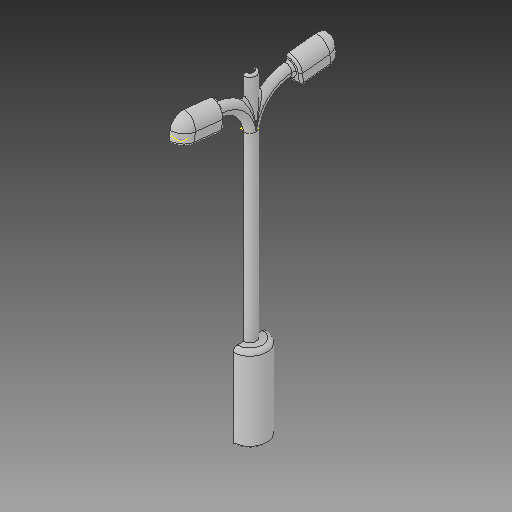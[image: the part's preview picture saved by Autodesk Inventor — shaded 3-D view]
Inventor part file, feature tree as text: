
AUTODESK INVENTOR PART (.ipt)
format: ipt  version: 2018 (Build 220112000, 112)  size: 484,864 bytes
history: native  units: mm
features: sketch x10, extrude x8, fillet x5, projected_geometry x3, plane x2, revolve x1, sweep x1, mirror x1
ambient origin geometry x8: Origin, YZ Plane, XZ Plane, XY Plane, X Axis, Y Axis, Z Axis, Center Point
bodies: Solid1 (feature_tree)
feature tree (31):
  revolve  "Revolution1"  [1 undecoded]
  fillet  "Fillet1"  Radius=8.0mm
  fillet  "Fillet2"  Radius=40.0mm
  fillet  "Fillet3"  [1 undecoded]
  plane  "Work Plane1"
  sweep  "Sweep1"
  extrude  "Extrusion2"  Depth=1.5mm
  fillet  "Fillet4"  Radius=1.0mm
  fillet  "Fillet5"  Radius=1.0mm
  extrude  "Extrusion3"  Depth=1.0mm
  extrude  "Extrusion4"  Depth=6.601018mm
  extrude  "Extrusion5"  Depth=1.0mm
  extrude  "Extrusion6"  [1 undecoded]
  extrude  "Extrusion7"  Depth=18.0mm
  plane  "Work Plane3"
  extrude  "Extrusion8"  TaperAngle=0.0deg  [1 undecoded]
  extrude  "Extrusion9"  Depth=10.0mm
  mirror  "Mirror1"
  sketch  "Sketch6"  dims[d0=150.0mm d1=3.0mm d3=8.0mm d4=40.0mm d5=90.0deg]
  sketch  "Sketch8"  dims[d20=1.5mm d21=1.5mm]
  sketch  "Sketch9"  dims[d22=1.5mm d23=1.0mm d24=1.0mm d25=1.0mm]
  projected_geometry  "Projected Loop3"
  sketch  "Sketch10"  dims[d26=1.0mm d27=1.0mm]
  projected_geometry  "Projected Loop4"
  sketch  "Sketch11"  dims[d28=1.456552mm d29=6.601018mm]
  sketch  "Sketch12"  dims[d30=2.0mm d31=1.0mm]
  sketch  "Sketch13"  dims[d32=1.0mm d33=-23.0mm]
  sketch  "Sketch14"  dims[d38=18.0mm d39=18.0mm]
  sketch  "Sketch15"  dims[d40=16.0mm d41=0.0mm d42=0.0mm]
  projected_geometry  "Projected Loop5"
  sketch  "Sketch16"  dims[d43=12.0mm d44=5.0mm d45=6.0mm d46=6.0mm d47=20.0mm d48=0.0mm d49=6.0mm d50=1.0mm d51=3.0mm d52=5.5mm d53=8.0mm d54=0.0mm d55=10.0mm d56=0.0mm d57=50.0mm d58=0.0mm d59=1.4mm d60=0.0mm d61=4.332171mm d62=15.0mm d63=0.0mm d64=-3.0mm d65=6.5mm d66=1.1mm d67=0.0mm d68=10.0mm d69=0.0mm]
note: 4 required parameter values undecoded (feature->parameter linkage not recoverable at this tier; creation-order binding heuristic only, values carry confidence <= 0.55)